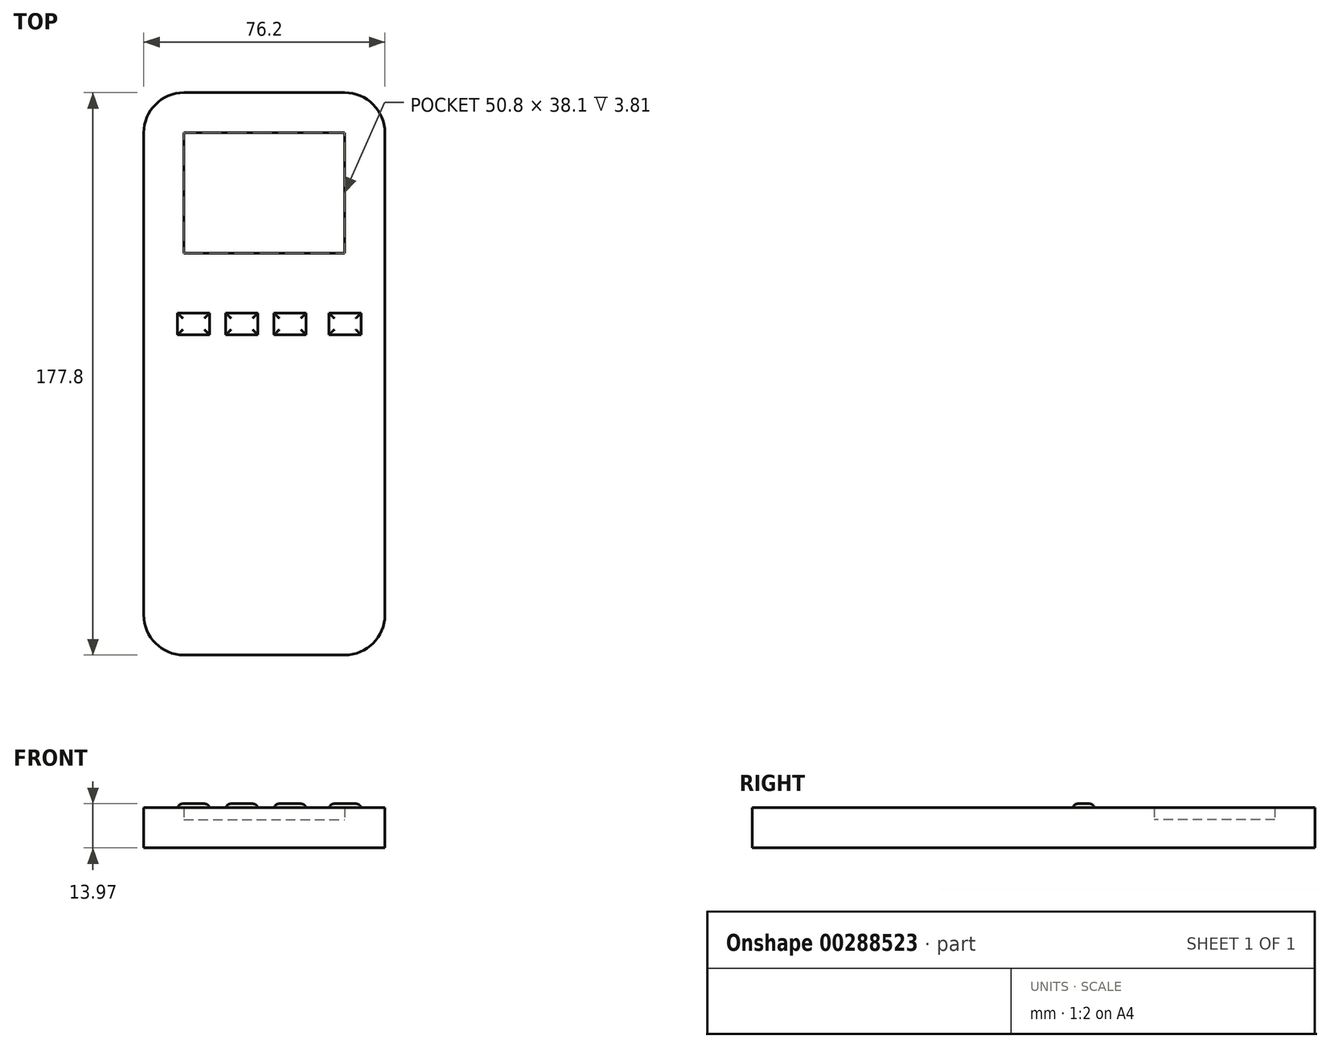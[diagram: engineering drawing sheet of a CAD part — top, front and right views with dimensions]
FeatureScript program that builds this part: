
annotation { "Feature Type Name" : "Feature", "Feature Type Description" : "" }
export const myFeature = defineFeature(function(context is Context, id is Id, definition is map)
    precondition{}
    {
        {
            var Q0;
            Q0=qCreatedBy(makeId("Top.planeOp"),FACE);
            var sketch = newSketch(context, id + "F0", { "sketchPlane" : qUnion([Q0])});
            skLineSegment(sketch, "E0.bottom", {"start": v(-36.7, 112.59) * mm, "end": v(14.1, 112.59) * mm});
            skLineSegment(sketch, "E0.top", {"start": v(-36.7, -65.21) * mm, "end": v(14.1, -65.21) * mm});
            skLineSegment(sketch, "E0.left", {"start": v(-49.4, 99.89) * mm, "end": v(-49.4, -52.51) * mm});
            skLineSegment(sketch, "E0.right", {"start": v(26.8, 99.89) * mm, "end": v(26.8, -52.51) * mm});
            skPoint(sketch, "E1.visualSharp", {"position": v(-49.4, -65.21) * mm});
            skArc(sketch, "E1.filletArc", {"start": v(-49.4, -52.51) * mm, "mid": v(-45.67, -61.5) * mm, "end": v(-36.7, -65.21) * mm});
            skPoint(sketch, "E2.visualSharp", {"position": v(26.8, -65.21) * mm});
            skArc(sketch, "E2.filletArc", {"start": v(14.1, -65.21) * mm, "mid": v(23.09, -61.5) * mm, "end": v(26.8, -52.51) * mm});
            skPoint(sketch, "E3.visualSharp", {"position": v(-49.4, 112.59) * mm});
            skArc(sketch, "E3.filletArc", {"start": v(-36.7, 112.59) * mm, "mid": v(-45.67, 108.87) * mm, "end": v(-49.4, 99.89) * mm});
            skPoint(sketch, "E4.visualSharp", {"position": v(26.8, 112.59) * mm});
            skArc(sketch, "E4.filletArc", {"start": v(26.8, 99.89) * mm, "mid": v(23.09, 108.87) * mm, "end": v(14.1, 112.59) * mm});
            skLineSegment(sketch, "E5.bottom", {"start": v(-36.7, 99.89) * mm, "end": v(14.1, 99.89) * mm});
            skLineSegment(sketch, "E5.top", {"start": v(-36.7, 61.79) * mm, "end": v(14.1, 61.79) * mm});
            skLineSegment(sketch, "E5.left", {"start": v(-36.7, 99.89) * mm, "end": v(-36.7, 61.79) * mm});
            skLineSegment(sketch, "E5.right", {"start": v(14.1, 99.89) * mm, "end": v(14.1, 61.79) * mm});
            skLineSegment(sketch, "E6", {"start": v(-49.4, 46.7) * mm, "end": v(26.8, 46.7) * mm});
            skSolve(sketch);
        }
        {
            var Q0;
            Q0=makeQuery(id+"F0.imprint","IMPRINT",FACE,{"disambiguationData":[TD([[makeQuery(id+"F0.imprint","IMPRINT",EDGE,{"derivedFrom":sQuery(id+"F0.wireOp",EDGE,"E0.top")}),1.0]])]});
            var Q1;
            Q1=makeQuery(id+"F0.imprint","IMPRINT",FACE,{"disambiguationData":[TD([[makeQuery(id+"F0.imprint","IMPRINT",EDGE,{"derivedFrom":sQuery(id+"F0.wireOp",EDGE,"E0.bottom")}),-1.0]])]});
            extrude(context, id + "F1", {"entities" : qUnion([Q0, Q1]), "depth" : 12.7 * mm});
        }
        {
            var Q0;
            Q0=makeQuery(id+"F0.imprint","IMPRINT",FACE,{"disambiguationData":[TD([[makeQuery(id+"F0.imprint","IMPRINT",EDGE,{"derivedFrom":sQuery(id+"F0.wireOp",EDGE,"E5.bottom")}),-1.0]])]});
            extrude(context, id + "F2", {"entities" : qUnion([Q0]), "operationType" : NewBodyOperationType.ADD, "depth" : 8.9 * mm});
        }
        {
            var Q0;
            Q0=makeQuery(id+"F1.opExtrude","CAP_FACE",FACE,{"disambiguationData":[OSD([sQuery(id+"F0.wireOp",EDGE,"E0.bottom"),sQuery(id+"F0.wireOp",EDGE,"E0.top"),sQuery(id+"F0.wireOp",EDGE,"E0.left"),sQuery(id+"F0.wireOp",EDGE,"E0.right"),sQuery(id+"F0.wireOp",EDGE,"E1.filletArc"),sQuery(id+"F0.wireOp",EDGE,"E2.filletArc"),sQuery(id+"F0.wireOp",EDGE,"E3.filletArc"),sQuery(id+"F0.wireOp",EDGE,"E4.filletArc"),sQuery(id+"F0.wireOp",EDGE,"E5.bottom"),sQuery(id+"F0.wireOp",EDGE,"E5.top"),sQuery(id+"F0.wireOp",EDGE,"E5.left"),sQuery(id+"F0.wireOp",EDGE,"E5.right")])],"isStart":false});
            var sketch = newSketch(context, id + "F3", { "sketchPlane" : qUnion([Q0])});
            skLineSegment(sketch, "E7.bottom", {"start": v(-38.72, 42.93) * mm, "end": v(-28.56, 42.93) * mm});
            skLineSegment(sketch, "E7.top", {"start": v(-38.72, 36) * mm, "end": v(-28.56, 36) * mm});
            skLineSegment(sketch, "E7.left", {"start": v(-38.72, 42.93) * mm, "end": v(-38.72, 36) * mm});
            skLineSegment(sketch, "E7.right", {"start": v(-28.56, 42.93) * mm, "end": v(-28.56, 36) * mm});
            skLineSegment(sketch, "E8.bottom", {"start": v(-23.48, 36) * mm, "end": v(-13.32, 36) * mm});
            skLineSegment(sketch, "E8.top", {"start": v(-23.48, 42.93) * mm, "end": v(-13.32, 42.93) * mm});
            skLineSegment(sketch, "E8.left", {"start": v(-23.48, 36) * mm, "end": v(-23.48, 42.93) * mm});
            skLineSegment(sketch, "E8.right", {"start": v(-13.32, 36) * mm, "end": v(-13.32, 42.93) * mm});
            skLineSegment(sketch, "E9.bottom", {"start": v(-8.24, 42.93) * mm, "end": v(1.92, 42.93) * mm});
            skLineSegment(sketch, "E9.top", {"start": v(-8.24, 36.02) * mm, "end": v(1.92, 36.02) * mm});
            skLineSegment(sketch, "E9.left", {"start": v(-8.24, 42.93) * mm, "end": v(-8.24, 36.02) * mm});
            skLineSegment(sketch, "E9.right", {"start": v(1.92, 42.93) * mm, "end": v(1.92, 36.02) * mm});
            skLineSegment(sketch, "E10.bottom", {"start": v(9.15, 42.93) * mm, "end": v(19.3, 42.93) * mm});
            skLineSegment(sketch, "E10.top", {"start": v(9.15, 36.02) * mm, "end": v(19.3, 36.02) * mm});
            skLineSegment(sketch, "E10.left", {"start": v(9.15, 42.93) * mm, "end": v(9.15, 36.02) * mm});
            skLineSegment(sketch, "E10.right", {"start": v(19.3, 42.93) * mm, "end": v(19.3, 36.02) * mm});
            skLineSegment(sketch, "E11.bottom", {"start": v(-38.72, 28.05) * mm, "end": v(-28.56, 28.05) * mm});
            skLineSegment(sketch, "E11.top", {"start": v(-38.72, 21.13) * mm, "end": v(-28.56, 21.13) * mm});
            skLineSegment(sketch, "E11.left", {"start": v(-38.72, 28.05) * mm, "end": v(-38.72, 21.13) * mm});
            skLineSegment(sketch, "E11.right", {"start": v(-28.56, 28.05) * mm, "end": v(-28.56, 21.13) * mm});
            skLineSegment(sketch, "E12.bottom", {"start": v(-23.48, 28.74) * mm, "end": v(-13.32, 28.74) * mm});
            skLineSegment(sketch, "E12.top", {"start": v(-23.48, 21.48) * mm, "end": v(-13.32, 21.48) * mm});
            skLineSegment(sketch, "E12.left", {"start": v(-23.48, 28.74) * mm, "end": v(-23.48, 21.48) * mm});
            skLineSegment(sketch, "E12.right", {"start": v(-13.32, 28.74) * mm, "end": v(-13.32, 21.48) * mm});
            skSolve(sketch);
        }
        {
            var Q0;
            Q0=makeQuery(id+"F3.imprint","IMPRINT",FACE,{"disambiguationData":[TD([[makeQuery(id+"F3.imprint","IMPRINT",EDGE,{"derivedFrom":sQuery(id+"F3.wireOp",EDGE,"E7.bottom")}),-1.0]])]});
            var Q1;
            Q1=makeQuery(id+"F3.imprint","IMPRINT",FACE,{"disambiguationData":[TD([[makeQuery(id+"F3.imprint","IMPRINT",EDGE,{"derivedFrom":sQuery(id+"F3.wireOp",EDGE,"E8.bottom")}),1.0]])]});
            var Q2;
            Q2=makeQuery(id+"F3.imprint","IMPRINT",FACE,{"disambiguationData":[TD([[makeQuery(id+"F3.imprint","IMPRINT",EDGE,{"derivedFrom":sQuery(id+"F3.wireOp",EDGE,"E9.bottom")}),-1.0]])]});
            var Q3;
            Q3=makeQuery(id+"F3.imprint","IMPRINT",FACE,{"disambiguationData":[TD([[makeQuery(id+"F3.imprint","IMPRINT",EDGE,{"derivedFrom":sQuery(id+"F3.wireOp",EDGE,"E10.bottom")}),-1.0]])]});
            extrude(context, id + "F4", {"entities" : qUnion([Q0, Q1, Q2, Q3]), "operationType" : NewBodyOperationType.ADD, "depth" : 1.27 * mm});
        }
        {
            var Q0;
            Q0=makeQuery(id+"F4.opExtrude","CAP_FACE",FACE,{"disambiguationData":[OSD([sQuery(id+"F3.wireOp",EDGE,"E7.bottom"),sQuery(id+"F3.wireOp",EDGE,"E7.top"),sQuery(id+"F3.wireOp",EDGE,"E7.left"),sQuery(id+"F3.wireOp",EDGE,"E7.right")])],"isStart":false});
            fillet(context, id + "F5", {"entities" : qUnion([Q0]), "radius" : 1.78 * mm, "allowEdgeOverflow" : false});
        }
        {
            var Q0;
            Q0=makeQuery(id+"F4.opExtrude","CAP_FACE",FACE,{"disambiguationData":[OSD([sQuery(id+"F3.wireOp",EDGE,"E8.bottom"),sQuery(id+"F3.wireOp",EDGE,"E8.top"),sQuery(id+"F3.wireOp",EDGE,"E8.left"),sQuery(id+"F3.wireOp",EDGE,"E8.right")])],"isStart":false});
            var Q1;
            Q1=makeQuery(id+"F4.opExtrude","CAP_EDGE",EDGE,{"disambiguationData":[OSD([sQuery(id+"F3.wireOp",EDGE,"E9.bottom")])],"isStart":false});
            var Q2;
            Q2=makeQuery(id+"F4.opExtrude","CAP_FACE",FACE,{"disambiguationData":[OSD([sQuery(id+"F3.wireOp",EDGE,"E10.bottom"),sQuery(id+"F3.wireOp",EDGE,"E10.top"),sQuery(id+"F3.wireOp",EDGE,"E10.left"),sQuery(id+"F3.wireOp",EDGE,"E10.right")])],"isStart":false});
            var Q3;
            Q3=makeQuery(id+"F4.opExtrude","CAP_FACE",FACE,{"disambiguationData":[OSD([sQuery(id+"F3.wireOp",EDGE,"E9.bottom"),sQuery(id+"F3.wireOp",EDGE,"E9.top"),sQuery(id+"F3.wireOp",EDGE,"E9.left"),sQuery(id+"F3.wireOp",EDGE,"E9.right")])],"isStart":false});
            fillet(context, id + "F6", {"entities" : qUnion([Q0, Q1, Q2, Q3]), "radius" : 1.78 * mm, "tangentPropagation" : true, "allowEdgeOverflow" : false});
        }
    });
